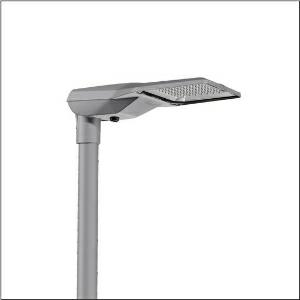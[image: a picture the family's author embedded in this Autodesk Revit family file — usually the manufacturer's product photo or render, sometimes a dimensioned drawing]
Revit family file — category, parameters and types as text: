
# Revit family: streetlight_sl_21_midi___st1_0a_5xe3d33r08nb_ea4c
name_source: partatom
category: Lighting Fixtures
units: mm (PartAtom-declared; Revit-internal decimal feet)

## family parameters
Cut with Voids When Loaded = No
Host = Face
Light Source = No
Part Type = Normal
Room Calculation Point = No
Round Connector Dimension = Use Diameter
Shared = No

## types (1)
- --- (1 x LED, 22700 lm, 151.2 W, 3000K)
    Apparent Load = 151 VA
    CIE Flux Codes = 40 73 97 100 100
    Color Rendering = 70
    Color Temperature = 3000K
    Default Elevation = 1800 mm
    Description = Streetlight SL 21 midi, mast luminaire, primary light control with lens, of PMMA, primary optical cover: cover, of toughened safety glass, transparent, light distribution: ST1.0a, light emission: direct distribution, primary light characteristic: asymmetric, installation type: side-entry, post-top, LED, High Power LED, rated luminous flux: 22.700lm, luminous efficacy: 150lm/W, light colour: 730, colour temperature: 3000K, control gear: D4i, control: flexible luminous flux parameterisation, time-dependent luminous flux control, constant luminous flux control, overheat protection, pre-setting: logarithmic dimming characteristic, mains connection: 230..240V, AC, 50/60Hz, start of lifetime: 151W, end of service life: 157W, reduction: 70W, luminaire housing, of diecast aluminium, powder-coated, Siteco® metallic grey (DB 702S), corrosivity category C5 mid according to DIN EN ISO 12944, please order mast flange separately, inclination adjustable: 0°, 5°, 10°, 15°, sealing non-destructively replaceable, multi-level sealing system, length: 644mm, width: 335mm, height: 110mm, mast flange for spigot size: 42mm (side-entry): 5XC10008XM4, 60/48mm (side-entry/post-top): 5XC10108XM2, 76/60mm (side-entry/post-top): 5XC10108XM1, mounting height: 4..8m, Smart Interface below, protection rating (complete): IP66, insulation class (complete): insulation class II (safety insulation), certification: CE, ENEC, ENEC+, VDE, impact resistance: IK10, permissible operating ambient temperature for outdoor applications: -40..+50°C, standard-compliant lighting for roads and squares, packaging unit: 1 piece

Light Distribution: ST1.0a
    Height = 111 mm
    Lamp = 1 x LED
    Lamp Light Flux = 22700 lm
    Lamp Power = 151.2 W
    Lamp count = 1
    Length = 644 mm
    Luminous efficacy = 150 lm/W
    Manufacturer = Siteco
    ModVariant = No
    Model = 5XE3D33R08NB
    Number of Poles = 1
    OnlyDefault = Yes
    Power Factor = 1
    Product Name = Streetlight SL 21 midi | ST1.0a
    Product group = mast luminaire | pylon top
    ProductGroupID = 6100
    Protection Class = Protection class II
    Protection Degree = IP 66
    RLX_Detail_Level = 1
    RLX_Emergency_Light_Flux = 0 lm
    RLX_Emergency_Type = 0
    RLX_Emergency_Type_DB = No
    RlxData = <blob elided: 27045 chars, md5=20c5f5b8>
    Socket = socket
    Standby Power = 0 W
    System Light Flux = 22700 lm
    System Power = 151 W
    Type Comments = factory setting: luminous flux: 100 % | dim-lin: 254 | 802 mA
    Type Image = l_1004300.jpg
    URL = http://relux.com
    VarID = @adj_170652
    Voltage = 0 V
    Weight = 0.00 kg
    Width = 336 mm

## geometry (parser evidence)
native form markers: Blend x4, Sweep x11
no freeform markers — native parametric forms only
